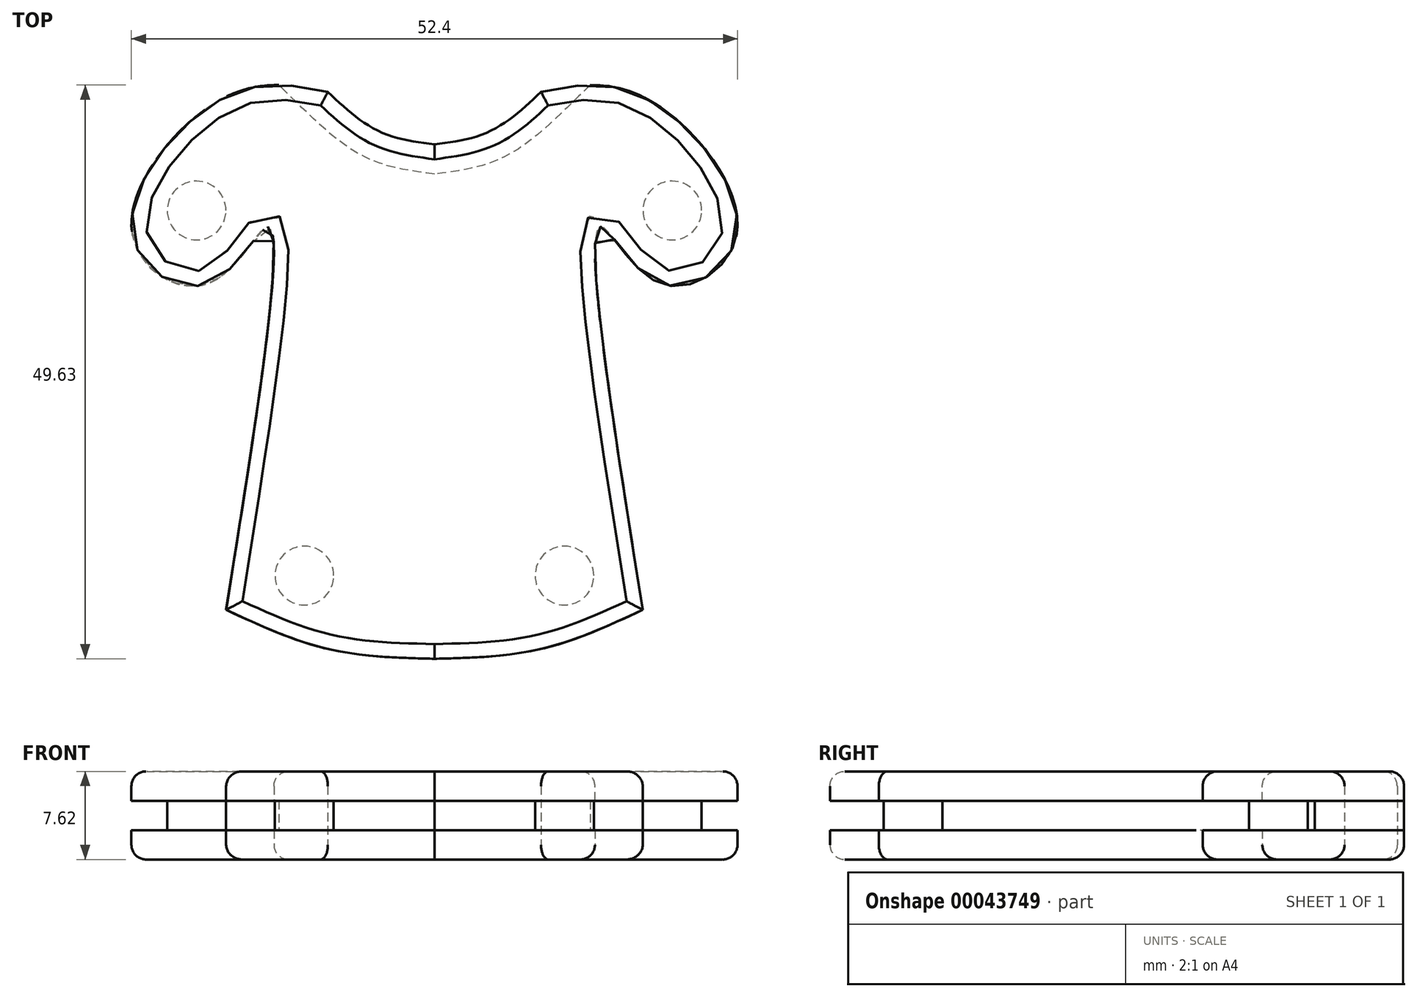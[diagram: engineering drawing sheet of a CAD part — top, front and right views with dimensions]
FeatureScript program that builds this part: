
annotation { "Feature Type Name" : "Feature", "Feature Type Description" : "" }
export const myFeature = defineFeature(function(context is Context, id is Id, definition is map)
    precondition{}
    {
        {
            var Q0;
            Q0=qCreatedBy(makeId("Top.planeOp"),FACE);
            var sketch = newSketch(context, id + "F0", { "sketchPlane" : qUnion([Q0])});
            skFitSpline(sketch, "E0", {"points": [v(-9.21, 26.75) * mm, v(-18.18, 26.24) * mm, v(-26.13, 14.4) * mm, v(-19.53, 10.17) * mm, v(-14.46, 15.07) * mm, v(-18, -18.08) * mm], "startDerivative": vector(-51.79, 10.4) * mm, "endDerivative": vector(-24.94, -156.76) * mm});
            skFitSpline(sketch, "E1", {"points": [v(-18, -18.08) * mm, v(-9.21, -21.46) * mm, v(0, -22.3) * mm], "startDerivative": vector(17.26, -8) * mm, "endDerivative": vector(18.76, -0.45) * mm});
            skFitSpline(sketch, "E2", {"points": [v(-9.21, 26.75) * mm, v(-4.48, 23.2) * mm, v(0, 22.19) * mm], "startDerivative": vector(8.65, -8.42) * mm, "endDerivative": vector(8.7, -1.3) * mm});
            skFitSpline(sketch, "E3.MirrorCS", {"points": [v(9.21, 26.75) * mm, v(4.48, 23.2) * mm, v(0, 22.19) * mm], "startDerivative": vector(-8.65, -8.42) * mm, "endDerivative": vector(-8.7, -1.3) * mm});
            skFitSpline(sketch, "E4.MirrorCS", {"points": [v(9.21, 26.75) * mm, v(18.18, 26.24) * mm, v(26.13, 14.4) * mm, v(19.53, 10.17) * mm, v(14.46, 15.07) * mm, v(18, -18.08) * mm], "startDerivative": vector(51.79, 10.4) * mm, "endDerivative": vector(24.94, -156.76) * mm});
            skFitSpline(sketch, "E5.MirrorCS", {"points": [v(18, -18.08) * mm, v(9.21, -21.46) * mm, v(0, -22.3) * mm], "startDerivative": vector(-17.26, -8) * mm, "endDerivative": vector(-18.76, -0.45) * mm});
            skSolve(sketch);
        }
        {
            var Q0;
            Q0 = qSketchRegion(id + "F0", true);
            extrude(context, id + "F1", {"entities" : qUnion([Q0]), "depth" : 7.62 * mm});
        }
        {
            var Q0;
            Q0=makeQuery(id+"F1.opExtrude","CAP_FACE",FACE,{"disambiguationData":[OSD([sQuery(id+"F0.wireOp",EDGE,"E0"),sQuery(id+"F0.wireOp",EDGE,"E1"),sQuery(id+"F0.wireOp",EDGE,"E2"),sQuery(id+"F0.wireOp",EDGE,"E3.MirrorCS"),sQuery(id+"F0.wireOp",EDGE,"E4.MirrorCS"),sQuery(id+"F0.wireOp",EDGE,"E5.MirrorCS")])],"isStart":true});
            var Q1;
            Q1=makeQuery(id+"F1.opExtrude","CAP_FACE",FACE,{"disambiguationData":[OSD([sQuery(id+"F0.wireOp",EDGE,"E0"),sQuery(id+"F0.wireOp",EDGE,"E1"),sQuery(id+"F0.wireOp",EDGE,"E2"),sQuery(id+"F0.wireOp",EDGE,"E3.MirrorCS"),sQuery(id+"F0.wireOp",EDGE,"E4.MirrorCS"),sQuery(id+"F0.wireOp",EDGE,"E5.MirrorCS")])],"isStart":false});
            fillet(context, id + "F2", {"entities" : qUnion([Q0, Q1]), "radius" : 1.27 * mm, "tangentPropagation" : true, "allowEdgeOverflow" : false});
        }
        {
            var Q0;
            Q0=makeQuery(id+"F1.opExtrude","CAP_FACE",FACE,{"disambiguationData":[OSD([sQuery(id+"F0.wireOp",EDGE,"E0"),sQuery(id+"F0.wireOp",EDGE,"E1"),sQuery(id+"F0.wireOp",EDGE,"E2"),sQuery(id+"F0.wireOp",EDGE,"E3.MirrorCS"),sQuery(id+"F0.wireOp",EDGE,"E4.MirrorCS"),sQuery(id+"F0.wireOp",EDGE,"E5.MirrorCS")])],"isStart":false});
            var sketch = newSketch(context, id + "F3", { "sketchPlane" : qUnion([Q0])});
            skCircle(sketch, "E6", {"center": v(-20.57, 16.48) * mm, "radius": 2.54 * mm});
            skCircle(sketch, "E7.MirrorC", {"center": v(20.57, 16.48) * mm, "radius": 2.54 * mm});
            skCircle(sketch, "E8", {"center": v(-11.25, -15.1) * mm, "radius": 2.54 * mm});
            skCircle(sketch, "E9.MirrorC", {"center": v(11.25, -15.1) * mm, "radius": 2.54 * mm});
            skSolve(sketch);
        }
        {
            var Q0;
            Q0=makeQuery(id+"F1.opExtrude","SWEPT_FACE",FACE,{"disambiguationData":[OSD([sQuery(id+"F0.wireOp",EDGE,"E0")])]});
            var Q1;
            Q1=makeQuery(id+"F1.opExtrude","SWEPT_FACE",FACE,{"disambiguationData":[OSD([sQuery(id+"F0.wireOp",EDGE,"E5.MirrorCS")])]});
            var Q2;
            Q2=makeQuery(id+"F1.opExtrude","SWEPT_FACE",FACE,{"disambiguationData":[OSD([sQuery(id+"F0.wireOp",EDGE,"E1")])]});
            var Q3;
            Q3=makeQuery(id+"F1.opExtrude","SWEPT_FACE",FACE,{"disambiguationData":[OSD([sQuery(id+"F0.wireOp",EDGE,"E4.MirrorCS")])]});
            shell(context, id + "F4", {"entities" : qUnion([Q0, Q1, Q2, Q3]), "thickness" : 2.54 * mm});
        }
        {
            var Q0;
            Q0 = qSketchRegion(id + "F3", true);
            extrude(context, id + "F5", {"entities" : qUnion([Q0]), "operationType" : NewBodyOperationType.ADD, "oppositeDirection" : true, "depth" : 7.62 * mm});
        }
    });
